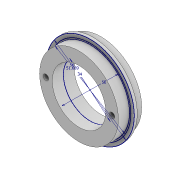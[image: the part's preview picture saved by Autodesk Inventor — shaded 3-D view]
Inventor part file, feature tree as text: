
AUTODESK INVENTOR PART (.ipt)
format: ipt  version: 2021 (Build 250183000, 183)  size: 125,440 bytes
history: native  units: mm
features: extrude x3, sketch x2, hole x2
ambient origin geometry x8: Origin, YZ Plane, XZ Plane, XY Plane, X Axis, Y Axis, Z Axis, Center Point
bodies: Solid1 (feature_tree)
feature tree (7):
  sketch  "Sketch1"  dims[d0=34.0mm d1=51.689mm]
  extrude  "Extrusion1"  Depth=51.689mm
  extrude  "Extrusion2"  Depth=4.0mm
  extrude  "Extrusion3"  Depth=7.0mm TaperAngle=0.0deg
  hole  "Hole1"  [1 undecoded]
  hole  "Hole2"  [1 undecoded]
  sketch  "Sketch2"  dims[d2=56.0mm d3=50.0mm d4=7.0mm d5=0.0mm d6=2.0mm d7=0.0mm d8=7.0mm d9=0.0mm d10=3.5mm d11=6.0mm d12=4.0mm d13=2.0mm d14=90.0deg d15=8.0mm d16=20.594885mm d17=3.5mm d18=6.0mm d19=6.5mm d20=4.0mm d21=90.0deg d22=8.0mm d23=20.594885mm]
note: 2 required parameter values undecoded (feature->parameter linkage not recoverable at this tier; creation-order binding heuristic only, values carry confidence <= 0.55)
